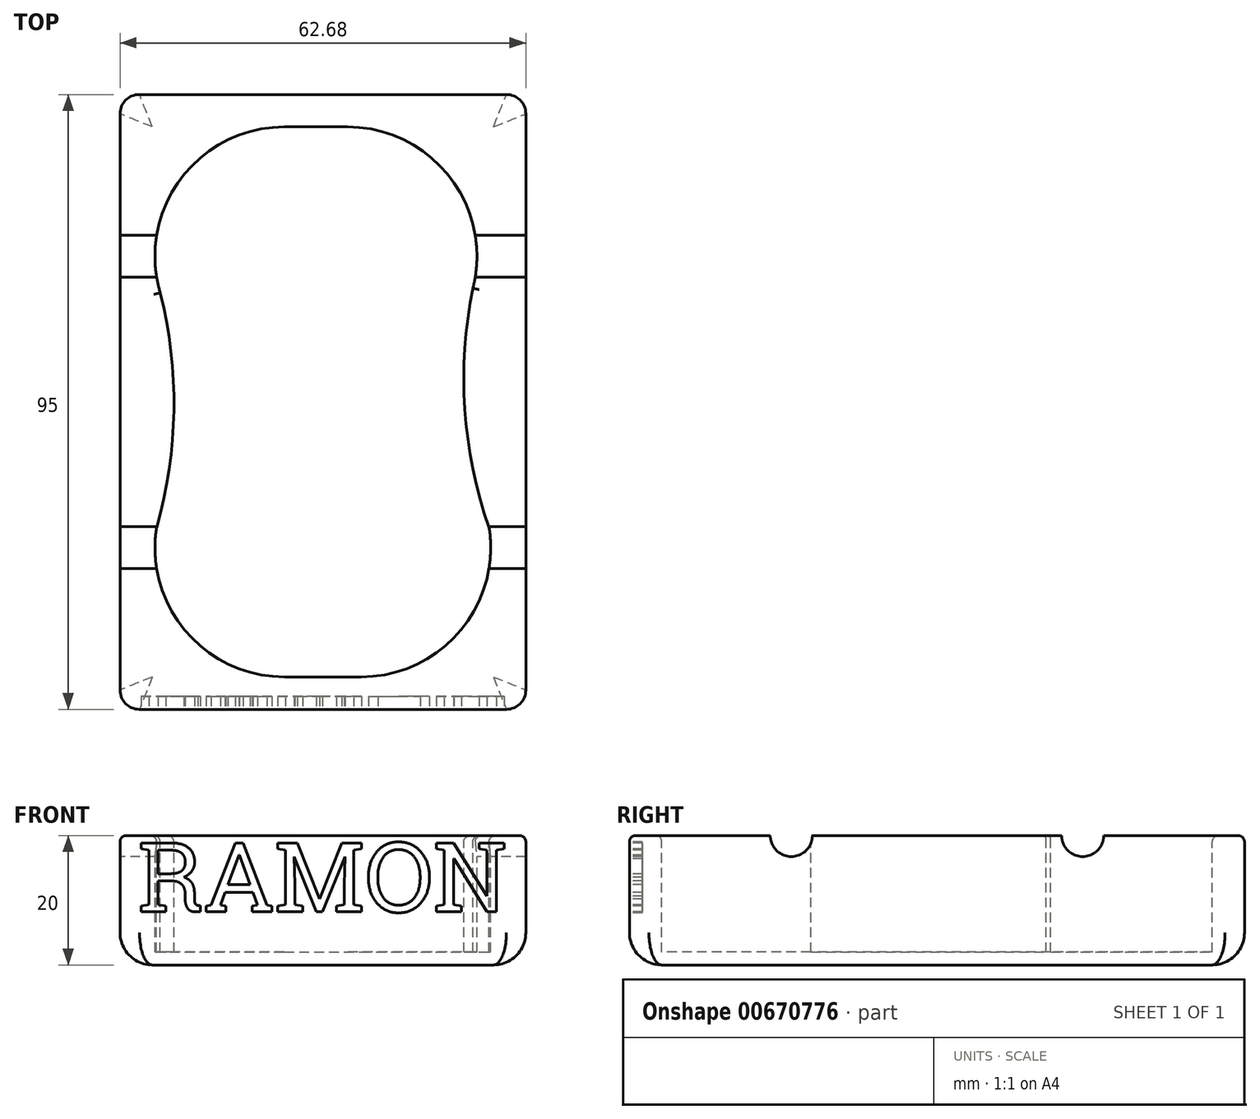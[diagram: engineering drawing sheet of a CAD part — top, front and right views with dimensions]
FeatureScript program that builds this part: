
annotation { "Feature Type Name" : "Feature", "Feature Type Description" : "" }
export const myFeature = defineFeature(function(context is Context, id is Id, definition is map)
    precondition{}
    {
        {
            var Q0;
            Q0=qCreatedBy(makeId("Top.planeOp"),FACE);
            cPlane(context, id + "F0", {"entities" : qUnion([Q0]), "cplaneType" : CPlaneType.OFFSET, "offset" : 20 * mm, "oppositeDirection" : true, "width" : 150 * mm, "height" : 150 * mm});
        }
        {
            var Q0;
            Q0=qCreatedBy(makeId("Top.planeOp"),FACE);
            var sketch = newSketch(context, id + "F1", { "sketchPlane" : qUnion([Q0])});
            skLineSegment(sketch, "E0", {"start": v(0, 122.9) * mm, "end": v(0, -122.9) * mm, "construction": true});
            skLineSegment(sketch, "E1", {"start": v(-122.9, 0) * mm, "end": v(122.9, 0) * mm, "construction": true});
            skLineSegment(sketch, "E2.bottom", {"start": v(20.4, 0) * mm, "end": v(32.25, 0) * mm});
            skLineSegment(sketch, "E2.top", {"start": v(20.4, 85) * mm, "end": v(30.12, 85) * mm});
            skPoint(sketch, "E3.visualSharp", {"position": v(0, 85) * mm});
            skArc(sketch, "E3.filletArc", {"start": v(20.4, 85) * mm, "mid": v(4.38, 76.99) * mm, "end": v(1.2, 59.37) * mm});
            skPoint(sketch, "E4.visualSharp", {"position": v(52, 85) * mm});
            skArc(sketch, "E4.filletArc", {"start": v(49.5, 60.06) * mm, "mid": v(45.91, 77.27) * mm, "end": v(30.12, 85) * mm});
            skPoint(sketch, "E5.visualSharp", {"position": v(0, 0) * mm});
            skArc(sketch, "E5.filletArc", {"start": v(0.63, 23.02) * mm, "mid": v(5.23, 6.97) * mm, "end": v(20.4, 0) * mm});
            skPoint(sketch, "E6.visualSharp", {"position": v(52, 0) * mm});
            skArc(sketch, "E6.filletArc", {"start": v(32.25, 0) * mm, "mid": v(47.42, 6.97) * mm, "end": v(52.02, 23.02) * mm});
            skArc(sketch, "E7", {"start": v(0.63, 23.02) * mm, "mid": v(3.32, 41.16) * mm, "end": v(1.2, 59.37) * mm});
            skArc(sketch, "E8", {"start": v(49.5, 60.06) * mm, "mid": v(48.26, 41.37) * mm, "end": v(52.02, 23.02) * mm});
            skLineSegment(sketch, "E9", {"start": v(98.15, 63.12) * mm, "end": v(98.15, 21.34) * mm});
            skArc(sketch, "E10", {"start": v(134, 85) * mm, "mid": v(110.9, 82.54) * mm, "end": v(98.15, 63.12) * mm});
            skLineSegment(sketch, "E11", {"start": v(98.15, 21.34) * mm, "end": v(108.03, 61.42) * mm});
            skArc(sketch, "E12", {"start": v(134, 85) * mm, "mid": v(117.41, 77.17) * mm, "end": v(108.03, 61.42) * mm});
            skSolve(sketch);
        }
        {
            var Q0;
            Q0=qCreatedBy(id+"F0.planeOp",FACE);
            var sketch = newSketch(context, id + "F2", { "sketchPlane" : qUnion([Q0])});
            skLineSegment(sketch, "E13.bottom", {"start": v(-5, 90) * mm, "end": v(57.68, 90) * mm});
            skLineSegment(sketch, "E13.top", {"start": v(-5, -5) * mm, "end": v(57.68, -5) * mm});
            skLineSegment(sketch, "E13.left", {"start": v(-5, 90) * mm, "end": v(-5, -5) * mm});
            skLineSegment(sketch, "E13.right", {"start": v(57.68, 90) * mm, "end": v(57.68, -5) * mm});
            skSolve(sketch);
        }
        {
            var Q0;
            Q0 = qSketchRegion(id + "F2", true);
            extrude(context, id + "F3", {"entities" : qUnion([Q0]), "depth" : 20 * mm, "offsetDistance" : 25 * mm});
        }
        {
            var Q0;
            Q0 = qSketchRegion(id + "F1", true);
            extrude(context, id + "F4", {"entities" : qUnion([Q0]), "operationType" : NewBodyOperationType.REMOVE, "oppositeDirection" : true, "depth" : 18 * mm, "offsetDistance" : 25 * mm});
        }
        {
            var Q0;
            Q0=makeQuery(id+"F3.opExtrude","SWEPT_EDGE",EDGE,{"disambiguationData":[OSD([sQuery(id+"F2.wireOp",EDGE,"E13.top"),sQuery(id+"F2.wireOp",EDGE,"E13.left")])]});
            fillet(context, id + "F5", {"entities" : qUnion([Q0]), "radius" : 3 * mm, "tangentPropagation" : true, "allowEdgeOverflow" : false});
        }
        {
            var Q0;
            Q0=makeQuery(id+"F3.opExtrude","SWEPT_EDGE",EDGE,{"disambiguationData":[OSD([sQuery(id+"F2.wireOp",EDGE,"E13.top"),sQuery(id+"F2.wireOp",EDGE,"E13.right")])]});
            fillet(context, id + "F6", {"entities" : qUnion([Q0]), "radius" : 3 * mm, "tangentPropagation" : true, "allowEdgeOverflow" : false});
        }
        {
            var Q0;
            Q0=makeQuery(id+"F3.opExtrude","SWEPT_EDGE",EDGE,{"disambiguationData":[OSD([sQuery(id+"F2.wireOp",EDGE,"E13.bottom"),sQuery(id+"F2.wireOp",EDGE,"E13.right")])]});
            fillet(context, id + "F7", {"entities" : qUnion([Q0]), "radius" : 3 * mm, "tangentPropagation" : true, "allowEdgeOverflow" : false});
        }
        {
            var Q0;
            Q0=makeQuery(id+"F3.opExtrude","SWEPT_EDGE",EDGE,{"disambiguationData":[OSD([sQuery(id+"F2.wireOp",EDGE,"E13.bottom"),sQuery(id+"F2.wireOp",EDGE,"E13.left")])]});
            fillet(context, id + "F8", {"entities" : qUnion([Q0]), "radius" : 3 * mm, "tangentPropagation" : true, "allowEdgeOverflow" : false});
        }
        {
            var Q0;
            Q0=makeQuery(id+"F3.opExtrude","CAP_FACE",FACE,{"disambiguationData":[OSD([sQuery(id+"F2.wireOp",EDGE,"E13.bottom"),sQuery(id+"F2.wireOp",EDGE,"E13.top"),sQuery(id+"F2.wireOp",EDGE,"E13.left"),sQuery(id+"F2.wireOp",EDGE,"E13.right")])],"isStart":false});
            fillet(context, id + "F9", {"entities" : qUnion([Q0]), "radius" : 1 * mm, "tangentPropagation" : true, "allowEdgeOverflow" : false});
        }
        {
            var Q0;
            Q0=makeQuery(id+"F3.opExtrude","SWEPT_FACE",FACE,{"disambiguationData":[OSD([sQuery(id+"F2.wireOp",EDGE,"E13.left")])]});
            fillet(context, id + "F10", {"entities" : qUnion([Q0]), "radius" : 5 * mm, "tangentPropagation" : true, "allowEdgeOverflow" : false});
        }
        {
            var Q0;
            Q0=makeQuery(id+"F3.opExtrude","SWEPT_FACE",FACE,{"disambiguationData":[OSD([sQuery(id+"F2.wireOp",EDGE,"E13.top")])]});
            var sketch = newSketch(context, id + "F11", { "sketchPlane" : qUnion([Q0])});
            skText(sketch, "E14", { "text": "RAMON", "fontName": "RobotoSlab-Regular.ttf"});
            const initialGuessF11  = {"E14": [-0.00227, -0.01179, 1, 0, 0.01079]};
            skSetInitialGuess(sketch, initialGuessF11);
            skSolve(sketch);
        }
        {
            var Q0;
            Q0 = qSketchRegion(id + "F11", true);
            extrude(context, id + "F12", {"entities" : qUnion([Q0]), "operationType" : NewBodyOperationType.REMOVE, "oppositeDirection" : true, "depth" : 2 * mm, "offsetDistance" : 25 * mm});
        }
        {
            var Q0;
            Q0=makeQuery(id+"F3.opExtrude","SWEPT_FACE",FACE,{"disambiguationData":[OSD([sQuery(id+"F2.wireOp",EDGE,"E13.left")])]});
            var sketch = newSketch(context, id + "F13", { "sketchPlane" : qUnion([Q0])});
            skCircle(sketch, "E15", {"center": v(-65, 0) * mm, "radius": 3.25 * mm});
            skCircle(sketch, "E16", {"center": v(-20, 0) * mm, "radius": 3.25 * mm});
            skSolve(sketch);
        }
        {
            var Q0;
            Q0 = qSketchRegion(id + "F13", true);
            extrude(context, id + "F14", {"entities" : qUnion([Q0]), "operationType" : NewBodyOperationType.REMOVE, "oppositeDirection" : true, "depth" : 70 * mm, "offsetDistance" : 25 * mm});
        }
    });
